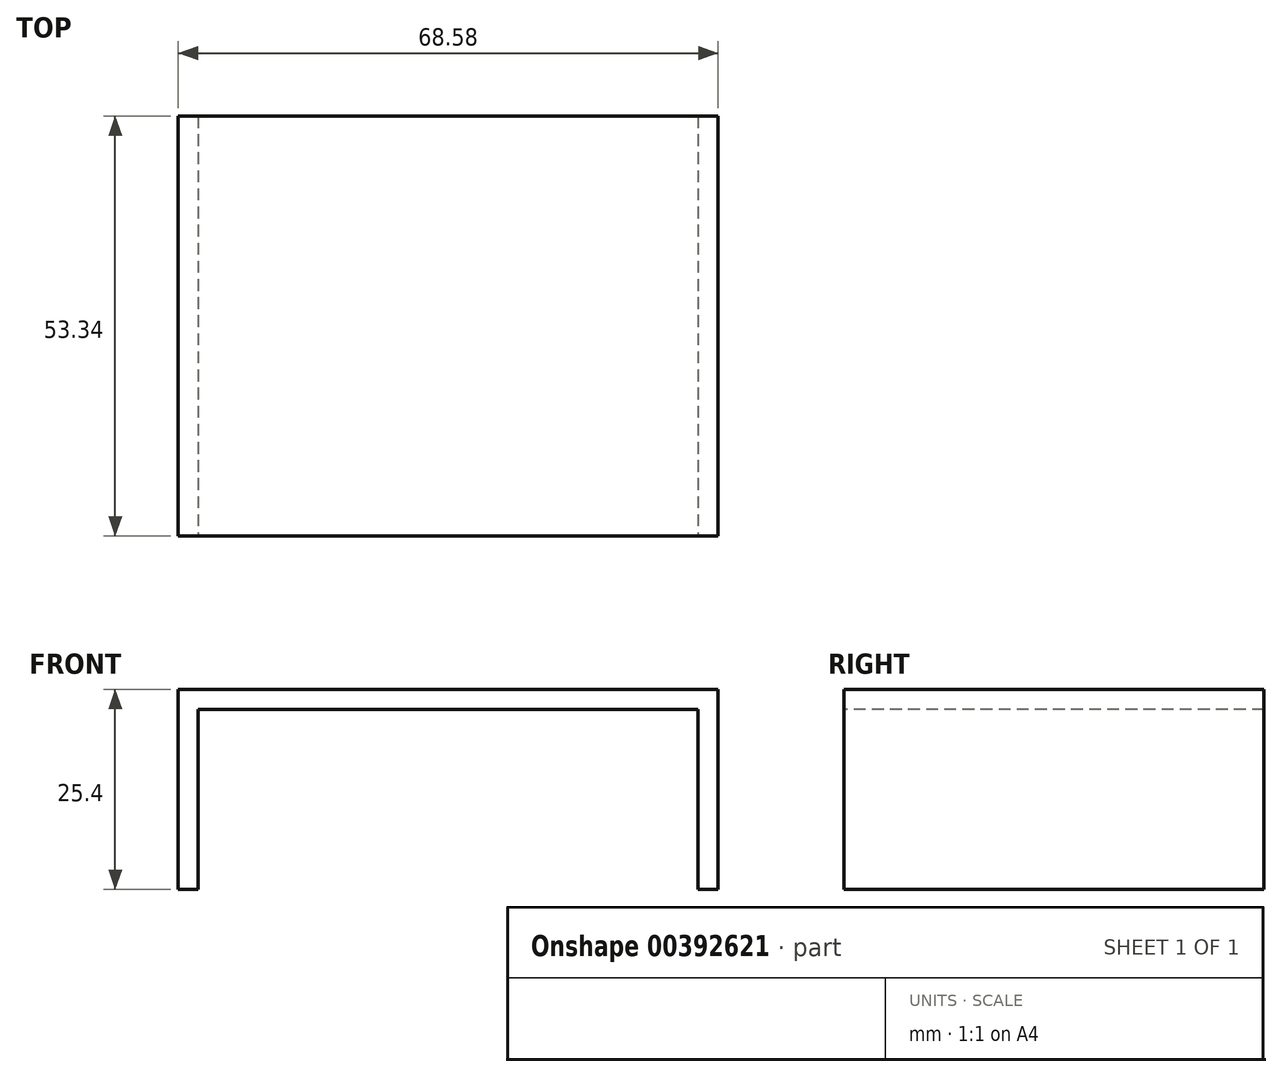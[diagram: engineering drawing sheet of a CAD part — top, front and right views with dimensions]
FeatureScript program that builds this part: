
annotation { "Feature Type Name" : "Feature", "Feature Type Description" : "" }
export const myFeature = defineFeature(function(context is Context, id is Id, definition is map)
    precondition{}
    {
        {
            var Q0;
            Q0=qCreatedBy(makeId("Top.planeOp"),FACE);
            var sketch = newSketch(context, id + "F0", { "sketchPlane" : qUnion([Q0])});
            skLineSegment(sketch, "E0.top", {"start": v(-34.3, -26.67) * mm, "end": v(34.29, -26.67) * mm});
            skLineSegment(sketch, "E0.left", {"start": v(-34.29, 26.67) * mm, "end": v(-34.3, -26.67) * mm});
            skLineSegment(sketch, "E0.right", {"start": v(34.3, 26.67) * mm, "end": v(34.29, -26.67) * mm});
            skPoint(sketch, "E0.middle", {"position": v(0, 0) * mm});
            skLineSegment(sketch, "E1", {"start": v(-34.3, 26.67) * mm, "end": v(-31.75, 26.67) * mm});
            skLineSegment(sketch, "E2", {"start": v(-31.75, 26.67) * mm, "end": v(-31.75, -26.67) * mm});
            skLineSegment(sketch, "E3", {"start": v(34.3, 26.67) * mm, "end": v(31.75, 26.67) * mm});
            skLineSegment(sketch, "E4", {"start": v(31.75, 26.67) * mm, "end": v(31.75, -26.67) * mm});
            skLineSegment(sketch, "E5", {"start": v(-31.75, 26.67) * mm, "end": v(31.75, 26.67) * mm});
            skLineSegment(sketch, "E6", {"start": v(31.75, -26.67) * mm, "end": v(29.2, -26.67) * mm});
            skLineSegment(sketch, "E7", {"start": v(29.2, -26.67) * mm, "end": v(29.2, 26.67) * mm});
            skLineSegment(sketch, "E8", {"start": v(-31.75, 26.67) * mm, "end": v(-29.21, 26.67) * mm});
            skLineSegment(sketch, "E9", {"start": v(-29.21, 26.67) * mm, "end": v(-29.2, -26.67) * mm});
            skSolve(sketch);
        }
        {
            var Q0;
            Q0 = qSketchRegion(id + "F0", true);
            extrude(context, id + "F1", {"entities" : qUnion([Q0]), "depth" : 25.4 * mm});
        }
        {
            var Q0;
            {var subQ0=sQuery(id+"F0.wireOp",EDGE,"E2");Q0=makeQuery(id+"F0.imprint","IMPRINT",FACE,{"disambiguationData":[TD([[makeQuery(id+"F0.imprint","IMPRINT",EDGE,{"derivedFrom":subQ0}),1.0]])]});}
            var Q1;
            {var subQ0=sQuery(id+"F0.wireOp",EDGE,"E4");Q1=makeQuery(id+"F0.imprint","IMPRINT",FACE,{"disambiguationData":[TD([[makeQuery(id+"F0.imprint","IMPRINT",EDGE,{"derivedFrom":subQ0}),-1.0]])]});}
            extrude(context, id + "F2", {"entities" : qUnion([Q0, Q1]), "operationType" : NewBodyOperationType.REMOVE, "depth" : 22.86 * mm});
        }
        {
            var Q0;
            {var subQ0=sQuery(id+"F0.wireOp",EDGE,"E7");Q0=makeQuery(id+"F0.imprint","IMPRINT",FACE,{"disambiguationData":[TD([[makeQuery(id+"F0.imprint","IMPRINT",EDGE,{"derivedFrom":subQ0}),1.0]])]});}
            extrude(context, id + "F3", {"entities" : qUnion([Q0]), "operationType" : NewBodyOperationType.REMOVE, "depth" : 22.86 * mm});
        }
    });
